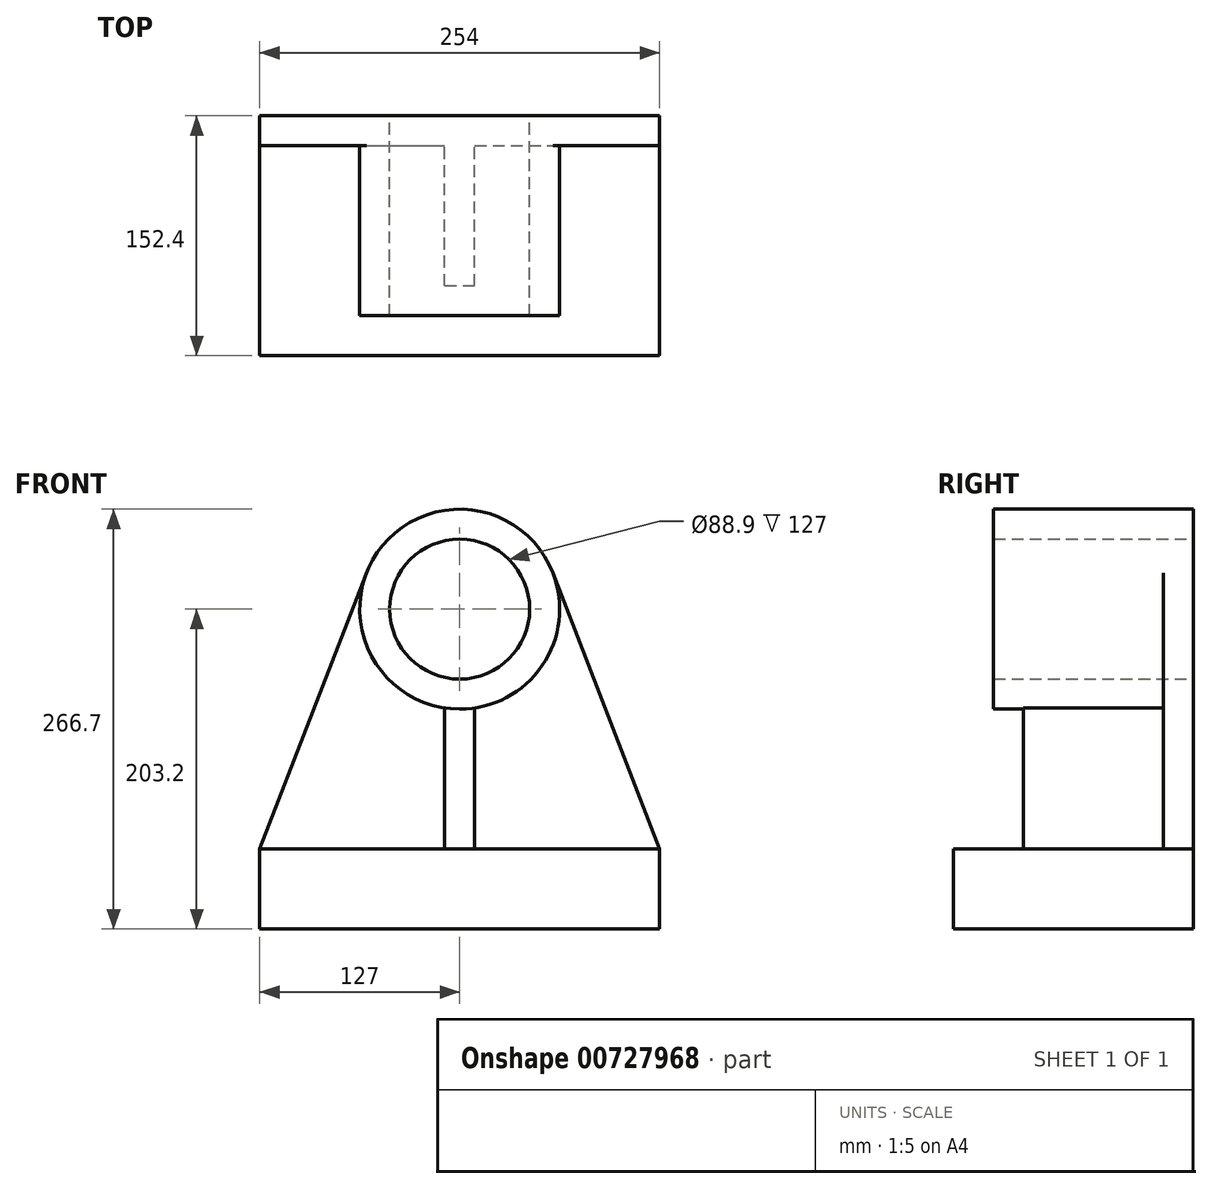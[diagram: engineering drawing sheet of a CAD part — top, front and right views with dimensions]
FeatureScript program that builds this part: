
annotation { "Feature Type Name" : "Feature", "Feature Type Description" : "" }
export const myFeature = defineFeature(function(context is Context, id is Id, definition is map)
    precondition{}
    {
        {
            var Q0;
            Q0=qCreatedBy(makeId("Front.planeOp"),FACE);
            var sketch = newSketch(context, id + "F0", { "sketchPlane" : qUnion([Q0])});
            skCircle(sketch, "E0", {"center": v(0, 0) * mm, "radius": 63.5 * mm});
            skCircle(sketch, "E1", {"center": v(0, 0) * mm, "radius": 44.45 * mm});
            skLineSegment(sketch, "E2", {"start": v(0, 0) * mm, "end": v(0, -177.8) * mm, "construction": true});
            skLineSegment(sketch, "E3.bottom", {"start": v(-127, -152.4) * mm, "end": v(127, -152.4) * mm});
            skLineSegment(sketch, "E3.top", {"start": v(-127, -203.2) * mm, "end": v(127, -203.2) * mm});
            skLineSegment(sketch, "E3.left", {"start": v(-127, -152.4) * mm, "end": v(-127, -203.2) * mm});
            skLineSegment(sketch, "E3.right", {"start": v(127, -152.4) * mm, "end": v(127, -203.2) * mm});
            skPoint(sketch, "E3.middle", {"position": v(0, -177.8) * mm});
            skLineSegment(sketch, "E4", {"start": v(-59.23, 22.9) * mm, "end": v(-127, -152.4) * mm});
            skLineSegment(sketch, "E5", {"start": v(59.23, 22.9) * mm, "end": v(127, -152.4) * mm});
            skLineSegment(sketch, "E6", {"start": v(-9.53, -62.78) * mm, "end": v(-9.52, -152.4) * mm});
            skLineSegment(sketch, "E7", {"start": v(9.52, -62.78) * mm, "end": v(9.53, -152.4) * mm});
            skArc(sketch, "E8", {"start": v(-59.23, 22.9) * mm, "mid": v(-54.93, -31.86) * mm, "end": v(-9.53, -62.78) * mm});
            skArc(sketch, "E9", {"start": v(59.23, 22.9) * mm, "mid": v(54.93, -31.86) * mm, "end": v(9.53, -62.78) * mm});
            skArc(sketch, "E10", {"start": v(-9.53, -62.78) * mm, "mid": v(0, -63.5) * mm, "end": v(9.53, -62.78) * mm});
            skLineSegment(sketch, "E11", {"start": v(-9.52, -152.4) * mm, "end": v(9.53, -152.4) * mm});
            skSolve(sketch);
        }
        {
            var Q0;
            Q0=makeQuery(id+"F0.imprint","IMPRINT",FACE,{"disambiguationData":[TD([[makeQuery(id+"F0.imprint","IMPRINT",EDGE,{"derivedFrom":sQuery(id+"F0.wireOp",EDGE,"E1")}),-1.0]])]});
            extrude(context, id + "F1", {"entities" : qUnion([Q0]), "depth" : 127 * mm, "offsetDistance" : 25.4 * mm});
        }
        {
            var Q0;
            {var subQ0=sQuery(id+"F0.wireOp",EDGE,"E5");Q0=makeQuery(id+"F0.imprint","IMPRINT",FACE,{"disambiguationData":[TD([[makeQuery(id+"F0.imprint","IMPRINT",EDGE,{"derivedFrom":subQ0}),-1.0]])]});}
            var Q1;
            {var subQ0=sQuery(id+"F0.wireOp",EDGE,"E4");Q1=makeQuery(id+"F0.imprint","IMPRINT",FACE,{"disambiguationData":[TD([[makeQuery(id+"F0.imprint","IMPRINT",EDGE,{"derivedFrom":subQ0}),1.0]])]});}
            extrude(context, id + "F2", {"entities" : qUnion([Q0, Q1]), "operationType" : NewBodyOperationType.ADD, "depth" : 19.05 * mm, "offsetDistance" : 25.4 * mm});
        }
        {
            var Q0;
            Q0=makeQuery(id+"F0.imprint","IMPRINT",FACE,{"disambiguationData":[TD([[makeQuery(id+"F0.imprint","IMPRINT",EDGE,{"derivedFrom":sQuery(id+"F0.wireOp",EDGE,"E3.top")}),1.0]])]});
            extrude(context, id + "F3", {"entities" : qUnion([Q0]), "operationType" : NewBodyOperationType.ADD, "depth" : 152.4 * mm, "offsetDistance" : 25.4 * mm});
        }
        {
            var Q0;
            {var subQ0=sQuery(id+"F0.wireOp",EDGE,"E6");Q0=makeQuery(id+"F0.imprint","IMPRINT",FACE,{"disambiguationData":[TD([[makeQuery(id+"F0.imprint","IMPRINT",EDGE,{"derivedFrom":subQ0}),1.0]])]});}
            extrude(context, id + "F4", {"entities" : qUnion([Q0]), "operationType" : NewBodyOperationType.ADD, "depth" : 107.95 * mm, "offsetDistance" : 25.4 * mm});
        }
    });
